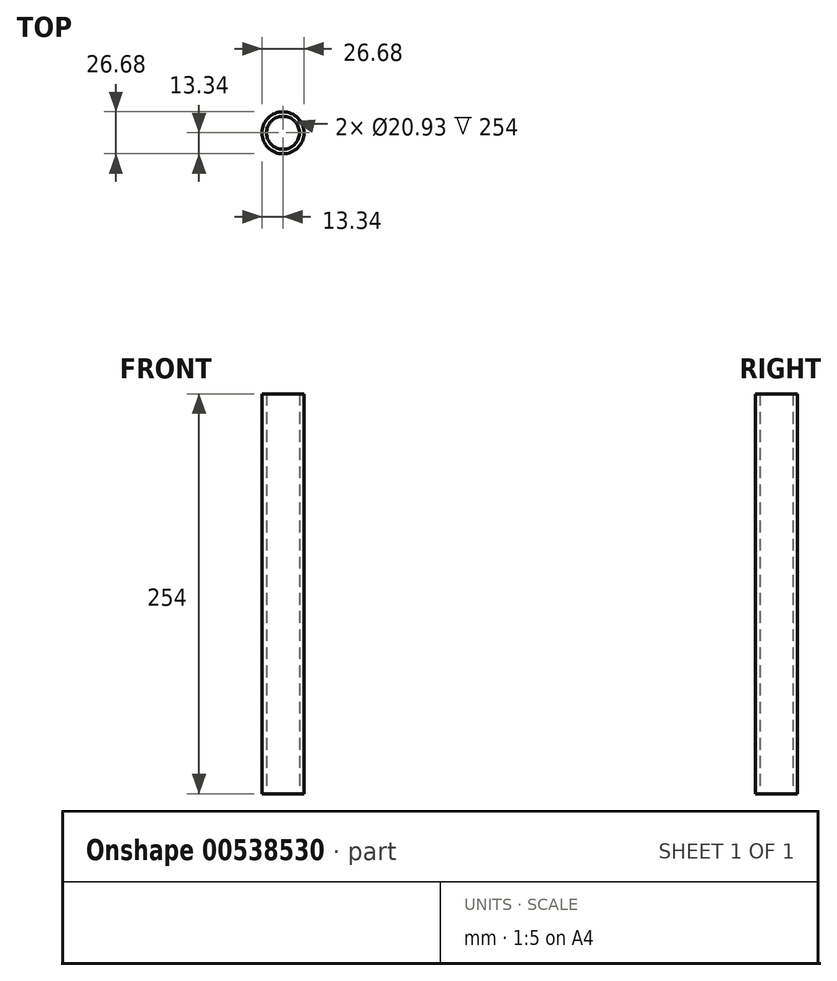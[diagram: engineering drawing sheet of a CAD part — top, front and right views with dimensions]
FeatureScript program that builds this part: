
annotation { "Feature Type Name" : "Feature", "Feature Type Description" : "" }
export const myFeature = defineFeature(function(context is Context, id is Id, definition is map)
    precondition{}
    {
        {
            var Q0;
            Q0=qCreatedBy(makeId("Top.planeOp"),FACE);
            var sketch = newSketch(context, id + "F0", { "sketchPlane" : qUnion([Q0])});
            skCircle(sketch, "E0", {"center": v(0, 0) * mm, "radius": 13.34 * mm});
            skCircle(sketch, "E1", {"center": v(0, 0) * mm, "radius": 10.46 * mm});
            skSolve(sketch);
        }
        {
            var Q0;
            Q0=makeQuery(id+"F0.imprint","IMPRINT",FACE,{"disambiguationData":[TD([[makeQuery(id+"F0.imprint","IMPRINT",EDGE,{"derivedFrom":sQuery(id+"F0.wireOp",EDGE,"E0")}),1.0]])]});
            extrude(context, id + "F1", {"entities" : qUnion([Q0]), "depth" : 254 * mm, "offsetDistance" : 25.4 * mm});
        }
        {
            var Q0;
            Q0=qCreatedBy(makeId("Front.planeOp"),FACE);
            cPlane(context, id + "F2", {"entities" : qUnion([Q0]), "cplaneType" : CPlaneType.OFFSET, "offset" : 15.24 * mm, "width" : 152.4 * mm, "height" : 152.4 * mm});
        }
    });
